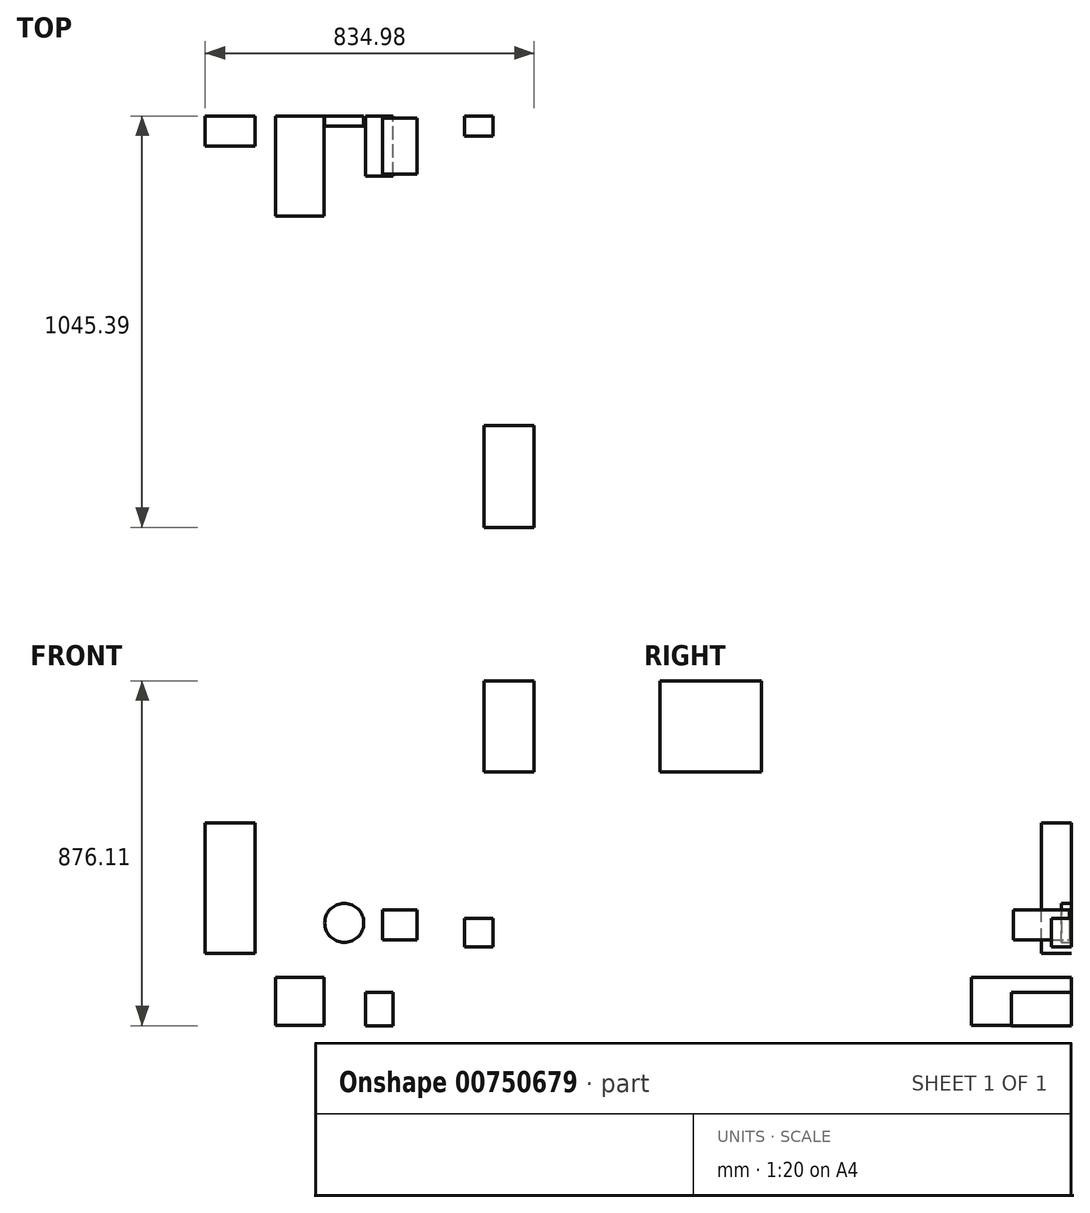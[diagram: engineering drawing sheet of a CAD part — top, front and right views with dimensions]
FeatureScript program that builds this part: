
annotation { "Feature Type Name" : "Feature", "Feature Type Description" : "" }
export const myFeature = defineFeature(function(context is Context, id is Id, definition is map)
    precondition{}
    {
        {
            var Q0;
            Q0=qCreatedBy(makeId("Front.planeOp"),FACE);
            var sketch = newSketch(context, id + "F0", { "sketchPlane" : qUnion([Q0])});
            skLineSegment(sketch, "E0.bottom", {"start": v(-49.34, 55.45) * mm, "end": v(23.23, 55.45) * mm});
            skLineSegment(sketch, "E0.top", {"start": v(-49.34, -17.88) * mm, "end": v(23.23, -17.88) * mm});
            skLineSegment(sketch, "E0.left", {"start": v(-49.34, 55.45) * mm, "end": v(-49.34, -17.88) * mm});
            skLineSegment(sketch, "E0.right", {"start": v(23.23, 55.45) * mm, "end": v(23.23, -17.88) * mm});
            skSolve(sketch);
        }
        {
            var Q0;
            Q0=makeQuery(id+"F0.imprint","IMPRINT",FACE,{"disambiguationData":[TD([[makeQuery(id+"F0.imprint","IMPRINT",EDGE,{"derivedFrom":sQuery(id+"F0.wireOp",EDGE,"E0.bottom")}),-1.0]])]});
            extrude(context, id + "F1", {"entities" : qUnion([Q0]), "depth" : 50.8 * mm, "offsetDistance" : 25.4 * mm});
        }
        {
            var Q0;
            Q0=qCreatedBy(makeId("Front.planeOp"),FACE);
            var sketch = newSketch(context, id + "F2", { "sketchPlane" : qUnion([Q0])});
            skLineSegment(sketch, "E1.bottom", {"start": v(-300.79, -132.36) * mm, "end": v(-231.63, -132.36) * mm});
            skLineSegment(sketch, "E1.top", {"start": v(-300.79, -217.56) * mm, "end": v(-231.63, -217.56) * mm});
            skLineSegment(sketch, "E1.left", {"start": v(-300.79, -132.36) * mm, "end": v(-300.79, -217.56) * mm});
            skLineSegment(sketch, "E1.right", {"start": v(-231.63, -132.36) * mm, "end": v(-231.63, -217.56) * mm});
            skSolve(sketch);
        }
        {
            var Q0;
            Q0=makeQuery(id+"F2.imprint","IMPRINT",FACE,{"disambiguationData":[TD([[makeQuery(id+"F2.imprint","IMPRINT",EDGE,{"derivedFrom":sQuery(id+"F2.wireOp",EDGE,"E1.bottom")}),-1.0]])]});
            extrude(context, id + "F3", {"entities" : qUnion([Q0]), "depth" : 152.4 * mm, "offsetDistance" : 25.4 * mm});
        }
        {
            var Q0;
            Q0=qCreatedBy(makeId("Top.planeOp"),FACE);
            var sketch = newSketch(context, id + "F4", { "sketchPlane" : qUnion([Q0])});
            skLineSegment(sketch, "E2.bottom", {"start": v(-257.34, -147.83) * mm, "end": v(-170.2, -147.83) * mm});
            skLineSegment(sketch, "E2.top", {"start": v(-257.34, -5.33) * mm, "end": v(-170.2, -5.33) * mm});
            skLineSegment(sketch, "E2.left", {"start": v(-257.34, -147.83) * mm, "end": v(-257.34, -5.33) * mm});
            skLineSegment(sketch, "E2.right", {"start": v(-170.2, -147.83) * mm, "end": v(-170.2, -5.33) * mm});
            skSolve(sketch);
        }
        {
            var Q0;
            Q0=makeQuery(id+"F4.imprint","IMPRINT",FACE,{"disambiguationData":[TD([[makeQuery(id+"F4.imprint","IMPRINT",EDGE,{"derivedFrom":sQuery(id+"F4.wireOp",EDGE,"E2.bottom")}),1.0]])]});
            extrude(context, id + "F5", {"entities" : qUnion([Q0]), "depth" : 76.2 * mm, "offsetDistance" : 25.4 * mm});
        }
        {
            var Q0;
            Q0=qCreatedBy(makeId("Front.planeOp"),FACE);
            var sketch = newSketch(context, id + "F6", { "sketchPlane" : qUnion([Q0])});
            skCircle(sketch, "E3", {"center": v(-354.95, 43.47) * mm, "radius": 49.61 * mm});
            skSolve(sketch);
        }
        {
            var Q0;
            Q0=makeQuery(id+"F6.imprint","IMPRINT",FACE,{"disambiguationData":[TD([[makeQuery(id+"F6.imprint","IMPRINT",EDGE,{"derivedFrom":sQuery(id+"F6.wireOp",EDGE,"E3")}),1.0]])]});
            extrude(context, id + "F7", {"entities" : qUnion([Q0]), "depth" : 25.4 * mm, "offsetDistance" : 25.4 * mm});
        }
        {
            var Q0;
            Q0=qCreatedBy(makeId("Front.planeOp"),FACE);
            var sketch = newSketch(context, id + "F8", { "sketchPlane" : qUnion([Q0])});
            skLineSegment(sketch, "E4.bottom", {"start": v(-529.87, -95.18) * mm, "end": v(-405.91, -95.18) * mm});
            skLineSegment(sketch, "E4.top", {"start": v(-529.87, -217.1) * mm, "end": v(-405.91, -217.1) * mm});
            skLineSegment(sketch, "E4.left", {"start": v(-529.87, -95.18) * mm, "end": v(-529.87, -217.1) * mm});
            skLineSegment(sketch, "E4.right", {"start": v(-405.91, -95.18) * mm, "end": v(-405.91, -217.1) * mm});
            skSolve(sketch);
        }
        {
            var Q0;
            Q0=makeQuery(id+"F8.imprint","IMPRINT",FACE,{"disambiguationData":[TD([[makeQuery(id+"F8.imprint","IMPRINT",EDGE,{"derivedFrom":sQuery(id+"F8.wireOp",EDGE,"E4.bottom")}),-1.0]])]});
            extrude(context, id + "F9", {"entities" : qUnion([Q0]), "depth" : 254 * mm, "offsetDistance" : 25.4 * mm});
        }
        {
            var Q0;
            Q0=qCreatedBy(makeId("Right.planeOp"),FACE);
            var sketch = newSketch(context, id + "F10", { "sketchPlane" : qUnion([Q0])});
            skLineSegment(sketch, "E5.bottom", {"start": v(-1045.4, 658.55) * mm, "end": v(-786.89, 658.55) * mm});
            skLineSegment(sketch, "E5.top", {"start": v(-1045.4, 427.26) * mm, "end": v(-786.89, 427.26) * mm});
            skLineSegment(sketch, "E5.left", {"start": v(-1045.4, 658.55) * mm, "end": v(-1045.4, 427.26) * mm});
            skLineSegment(sketch, "E5.right", {"start": v(-786.89, 658.55) * mm, "end": v(-786.89, 427.26) * mm});
            skSolve(sketch);
        }
        {
            var Q0;
            Q0=makeQuery(id+"F10.imprint","IMPRINT",FACE,{"disambiguationData":[TD([[makeQuery(id+"F10.imprint","IMPRINT",EDGE,{"derivedFrom":sQuery(id+"F10.wireOp",EDGE,"E5.bottom")}),-1.0]])]});
            extrude(context, id + "F11", {"entities" : qUnion([Q0]), "depth" : 127 * mm, "offsetDistance" : 25.4 * mm});
        }
        {
            var Q0;
            Q0=qCreatedBy(makeId("Front.planeOp"),FACE);
            var sketch = newSketch(context, id + "F12", { "sketchPlane" : qUnion([Q0])});
            skLineSegment(sketch, "E6.bottom", {"start": v(-707.98, -33.83) * mm, "end": v(-582.14, -33.83) * mm});
            skLineSegment(sketch, "E6.top", {"start": v(-707.98, 297.93) * mm, "end": v(-582.14, 297.93) * mm});
            skLineSegment(sketch, "E6.left", {"start": v(-707.98, -33.83) * mm, "end": v(-707.98, 297.93) * mm});
            skLineSegment(sketch, "E6.right", {"start": v(-582.14, -33.83) * mm, "end": v(-582.14, 297.93) * mm});
            skSolve(sketch);
        }
        {
            var Q0;
            Q0=makeQuery(id+"F12.imprint","IMPRINT",FACE,{"disambiguationData":[TD([[makeQuery(id+"F12.imprint","IMPRINT",EDGE,{"derivedFrom":sQuery(id+"F12.wireOp",EDGE,"E6.bottom")}),1.0]])]});
            extrude(context, id + "F13", {"entities" : qUnion([Q0]), "depth" : 76.2 * mm, "offsetDistance" : 25.4 * mm});
        }
    });
